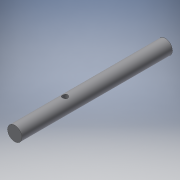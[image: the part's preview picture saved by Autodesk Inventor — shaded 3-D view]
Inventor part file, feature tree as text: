
AUTODESK INVENTOR PART (.ipt)
format: ipt  version: 2017 (Build 210142000, 142)  size: 101,888 bytes
history: native  units: in
note: dims shown in document units (in); Inventor stores cm internally (conversion verified against a paired STEP export)
features: extrude x2, sketch x2
ambient origin geometry x8: Origin, YZ Plane, XZ Plane, XY Plane, X Axis, Y Axis, Z Axis, Center Point
bodies: Solid1 (feature_tree)
feature tree (4):
  extrude  "Extrusion1"  Depth=3.3071in TaperAngle=0.0deg
  extrude  "Extrusion2"  Depth=2.2047in TaperAngle=0.0deg
  sketch  "Sketch1"  dims[d0=0.315in d1=3.3071in d2=0.0in]
  sketch  "Sketch2"  dims[d3=0.1181in d5=3.937in d6=0.0in d7=2.2047in]
